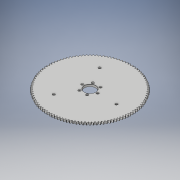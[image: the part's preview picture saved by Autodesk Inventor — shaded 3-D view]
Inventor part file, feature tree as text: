
AUTODESK INVENTOR PART (.ipt)
format: ipt  version: 2019 (Build 230136000, 136)  size: 1,399,808 bytes
history: native  units: mm
features: sketch x3, projected_geometry x2, other x1, hole x1, extrude x1, pattern_circular x1
ambient origin geometry x8: Origin, YZ Plane, XZ Plane, XY Plane, X Axis, Y Axis, Z Axis, Center Point
bodies: Solide1 (feature_tree)
feature tree (9):
  other  "Révolution1"
  hole  "Perçage1"  [1 undecoded]
  extrude  "Extrusion1"  Depth=0.5mm
  pattern_circular  "Réseau circulaire1"  [2 undecoded]
  sketch  "Esquisse1"
  sketch  "Esquisse2"
  sketch  "Esquisse3"
  projected_geometry  "Boucle projetée1"
  projected_geometry  "Boucle projetée2"
note: 3 required parameter values undecoded (feature->parameter linkage not recoverable at this tier; creation-order binding heuristic only, values carry confidence <= 0.55)
